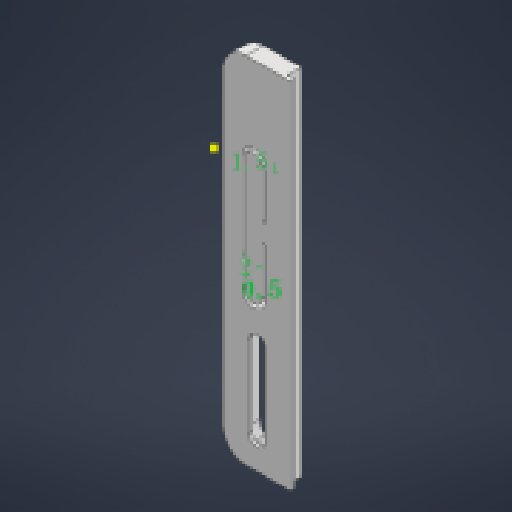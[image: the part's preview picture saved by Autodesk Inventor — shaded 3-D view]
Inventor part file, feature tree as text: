
AUTODESK INVENTOR PART (.ipt)
format: ipt  version: 2025 (Build 290162000, 162)  size: 424,960 bytes
history: native  units: mm
features: extrude x13, sketch x12, reference x12, other x11, projected_geometry x6, fillet x3, plane x1
ambient origin geometry x8: Origin, YZ Plane, XZ Plane, XY Plane, X Axis, Y Axis, Z Axis, Center Point
bodies: 实体1 (feature_tree)
feature tree (58):
  extrude  "拉伸1"  Depth=10.0mm TaperAngle=0.0deg
  sketch  "草图2"  dims[d4=10.0mm d5=0.0mm d6=0.2mm]
  plane  "工作平面1"
  extrude  "拉伸2"  Depth=10.0mm
  extrude  "拉伸3"  Depth=0.4mm TaperAngle=0.0deg
  extrude  "拉伸4"  Depth=3.4mm
  sketch  "草图5"  dims[d14=1.0mm d15=3.9mm d16=0.0mm]
  extrude  "拉伸5"  Depth=3.9mm TaperAngle=0.0deg
  extrude  "拉伸6"  Depth=4.5mm
  extrude  "拉伸7"  Depth=4.5mm TaperAngle=0.0deg
  fillet  "圆角1"  Radius=0.2mm
  fillet  "圆角2"  Radius=1.0mm
  extrude  "拉伸8"  Depth=1.1mm TaperAngle=0.0deg
  fillet  "圆角3"  Radius=0.2mm
  extrude  "拉伸10"  Depth=1.1mm TaperAngle=0.0deg
  other  "直接编辑1"
  extrude  "拉伸11"  Depth=1.5mm
  extrude  "拉伸12"  Depth=4.0mm TaperAngle=0.0deg
  extrude  "拉伸13"  Depth=2.0mm
  extrude  "拉伸14"  Depth=6.0mm TaperAngle=0.0deg
  other  "直接编辑3"
  sketch  "草图1"  dims[d0=3.0mm d1=0.0mm d2=10.0mm d3=0.0mm]
  reference  "参考1"
  reference  "参考2"
  reference  "参考3"
  reference  "参考4"
  reference  "参考5"
  reference  "参考6"
  sketch  "草图3"  dims[d7=0.2mm d8=0.4mm d9=0.0mm]
  reference  "参考8"
  reference  "参考9"
  sketch  "草图4"  dims[d11=20.4mm d13=3.4mm]
  projected_geometry  "投影回路1"
  sketch  "草图8"  dims[d18=0.5mm d19=0.0mm d20=4.5mm]
  reference  "参考11"
  reference  "参考12"
  projected_geometry  "投影回路2"
  sketch  "草图11"  dims[d21=4.5mm d22=1.5mm d23=0.0mm d24=0.2mm d25=1.0mm]
  sketch  "草图12"  dims[d26=1.5mm d27=1.1mm d28=0.0mm d29=0.2mm]
  reference  "参考13"
  reference  "参考14"
  sketch  "草图13"  dims[d33=2.0mm d35=1.1mm d36=0.0mm]
  projected_geometry  "投影回路3"
  projected_geometry  "投影回路4"
  projected_geometry  "投影回路5"
  sketch  "草图14"  dims[d37=0.0mm d38=0.0mm d39=-0.5mm d41=1.5mm]
  projected_geometry  "投影回路6"
  sketch  "草图15"  dims[d42=0.5mm d43=4.0mm d44=0.0mm]
  sketch  "草图16"  dims[d45=15.0mm d46=0.0mm d47=2.0mm d48=6.0mm d49=0.0mm d50=4.0mm d51=0.0mm d52=0.5mm d53=0.872665mm]
  parser-record x2  (decoder bookkeeping rows leaked as tree rows — omitted from the tree; the rows remain in map.json)
  other  "装配体.iam"
  other  "键盘外壳:1"
  other  "dlc.iam"
  other  "指纹识别:1"
  other  "音量接口:1"
  other  "移动1"
  other  "删除2"
note: 2 file-system paths scrubbed to <path> (originals preserved in map.json)
